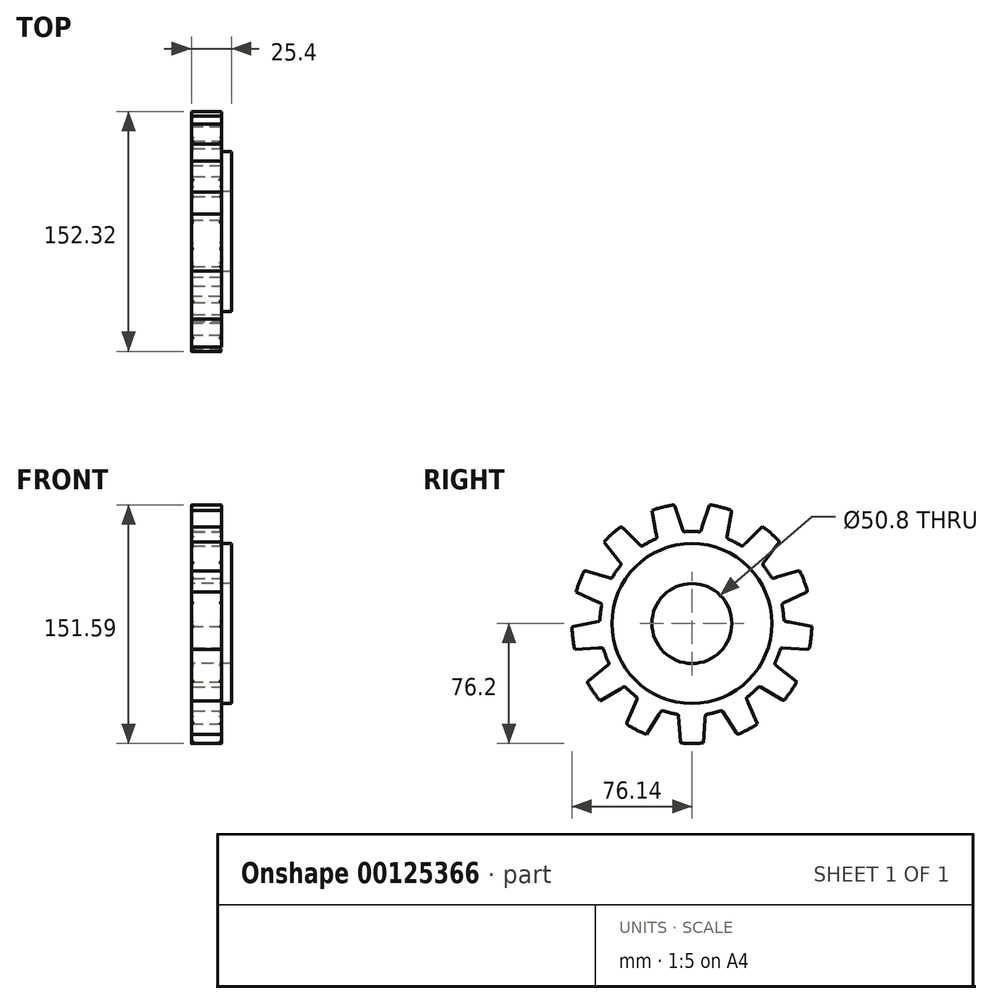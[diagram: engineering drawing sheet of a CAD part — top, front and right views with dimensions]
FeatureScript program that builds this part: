
annotation { "Feature Type Name" : "Feature", "Feature Type Description" : "" }
export const myFeature = defineFeature(function(context is Context, id is Id, definition is map)
    precondition{}
    {
        {
            var Q0;
            Q0=qCreatedBy(makeId("Front.planeOp"),FACE);
            var sketch = newSketch(context, id + "F0", { "sketchPlane" : qUnion([Q0])});
            skLineSegment(sketch, "E0.bottom", {"start": v(-41.26, 25.4) * mm, "end": v(-22.2, 25.4) * mm});
            skLineSegment(sketch, "E0.left", {"start": v(-41.26, 25.4) * mm, "end": v(-41.26, -25.4) * mm});
            skLineSegment(sketch, "E0.right", {"start": v(-22.2, 25.4) * mm, "end": v(-22.2, 0) * mm});
            skLineSegment(sketch, "E1.top", {"start": v(-22.2, 0) * mm, "end": v(-15.86, 0) * mm});
            skLineSegment(sketch, "E1.right", {"start": v(-15.86, -25.4) * mm, "end": v(-15.86, 0) * mm});
            skLineSegment(sketch, "E2", {"start": v(-57.48, -50.8) * mm, "end": v(16.42, -50.8) * mm});
            skLineSegment(sketch, "E3", {"start": v(-41.26, -25.4) * mm, "end": v(-15.86, -25.4) * mm});
            skSolve(sketch);
        }
        {
            var Q0;
            Q0=makeQuery(id+"F0.imprint","IMPRINT",FACE,{"disambiguationData":[TD([[makeQuery(id+"F0.imprint","IMPRINT",EDGE,{"derivedFrom":sQuery(id+"F0.wireOp",EDGE,"E0.bottom")}),-1.0]])]});
            var Q1;
            Q1=sQuery(id+"F0.wireOp",EDGE,"E2");
            revolve(context, id + "F1", {"entities" : qUnion([Q0]), "axis" : qUnion([Q1]), "revolveType" : RevolveType.FULL});
        }
        {
            var Q0;
            Q0=makeQuery(id+"F1.opRevolve","SWEPT_FACE",FACE,{"disambiguationData":[OSD([sQuery(id+"F0.wireOp",EDGE,"E0.right")])]});
            var sketch = newSketch(context, id + "F2", { "sketchPlane" : qUnion([Q0])});
            skLineSegment(sketch, "E4", {"start": v(-11.09, 24.59) * mm, "end": v(-5.53, 7.37) * mm});
            skLineSegment(sketch, "E5.MirrorCS", {"start": v(11.09, 24.59) * mm, "end": v(5.53, 7.37) * mm});
            skPoint(sketch, "E6.start.orphan", {"position": v(0, 25.4) * mm});
            skArc(sketch, "E7", {"start": v(5.53, 7.37) * mm, "mid": v(0, 7.63) * mm, "end": v(-5.53, 7.37) * mm});
            skSolve(sketch);
        }
        {
            var Q0;
            {var subQ0=sQuery(id+"F2.wireOp",EDGE,"E4");Q0=makeQuery(id+"F2.imprint","IMPRINT",FACE,{"disambiguationData":[TD([[makeQuery(id+"F2.imprint","IMPRINT",EDGE,{"derivedFrom":subQ0}),1.0]])]});}
            extrude(context, id + "F3", {"entities" : qUnion([Q0]), "operationType" : NewBodyOperationType.REMOVE, "oppositeDirection" : true, "depth" : 25.4 * mm});
        }
        {
            var Q0;
            Q0=makeQuery(id+"F3.boolean.opBoolean","COPY",FACE,{"derivedFrom":makeQuery(id+"F3.opExtrude","SWEPT_FACE",FACE,{"disambiguationData":[OSD([sQuery(id+"F2.wireOp",EDGE,"E4")])]})});
            var Q1;
            Q1=makeQuery(id+"F3.boolean.opBoolean","COPY",FACE,{"derivedFrom":makeQuery(id+"F3.opExtrude","SWEPT_FACE",FACE,{"disambiguationData":[OSD([sQuery(id+"F2.wireOp",EDGE,"E7")])]})});
            var Q2;
            Q2=makeQuery(id+"F3.boolean.opBoolean","INTERSECT",EDGE,{"derivedFrom":[makeQuery(id+"F1.opRevolve","SWEPT_FACE",FACE,{"disambiguationData":[OSD([sQuery(id+"F0.wireOp",EDGE,"E0.left")])]}),makeQuery(id+"F3.opExtrude","SWEPT_FACE",FACE,{"disambiguationData":[OSD([sQuery(id+"F2.wireOp",EDGE,"E7")])]})]});
            fillet(context, id + "F4", {"entities" : qUnion([Q0, Q1, Q2]), "radius" : 1.27 * mm, "tangentPropagation" : true, "allowEdgeOverflow" : false});
        }
        {
            var Q0;
            Q0=makeQuery(id+"F3.boolean.opBoolean","COPY",FACE,{"derivedFrom":makeQuery(id+"F3.opExtrude","SWEPT_FACE",FACE,{"disambiguationData":[OSD([sQuery(id+"F2.wireOp",EDGE,"E4")])]})});
            var Q1;
            Q1=makeQuery(id+"F4.opFillet","BLEND_FACE",FACE,{"disambiguationData":[OSD([sQuery(id+"F2.wireOp",EDGE,"E4")])]});
            var Q2;
            Q2=makeQuery(id+"F4.opFillet","BLEND_FACE",FACE,{"disambiguationData":[OSD([sQuery(id+"F0.wireOp",EDGE,"E0.bottom"),sQuery(id+"F0.wireOp",EDGE,"E0.right"),sQuery(id+"F2.wireOp",EDGE,"E4")])]});
            var Q3;
            {var subQ0=sQuery(id+"F2.wireOp",EDGE,"E7");var subQ1=sQuery(id+"F2.wireOp",EDGE,"E4");Q3=makeQuery(id+"F4.opFillet","BLEND_FACE",FACE,{"disambiguationData":[OSD([subQ1,subQ0]),TDD([makeQuery(id+"F3.boolean.opBoolean","COPY",EDGE,{"derivedFrom":makeQuery(id+"F3.opExtrude","SWEPT_EDGE",EDGE,{"disambiguationData":[OSD([subQ1,subQ0])]})})])]});}
            var Q4;
            {var subQ0=sQuery(id+"F2.wireOp",EDGE,"E7");var subQ1=sQuery(id+"F2.wireOp",EDGE,"E4");Q4=makeQuery(id+"F4.opFillet","BLEND_FACE",FACE,{"disambiguationData":[OSD([subQ1,subQ0]),TDD([makeQuery(id+"F3.boolean.opBoolean","COPY",VERTEX,{"derivedFrom":makeQuery(id+"F3.opExtrude","CAP_VERTEX",VERTEX,{"disambiguationData":[OSD([subQ1,subQ0])],"isStart":true})})])]});}
            var Q5;
            Q5=makeQuery(id+"F4.opFillet","BLEND_FACE",FACE,{"disambiguationData":[OSD([sQuery(id+"F2.wireOp",EDGE,"E7")])]});
            var Q6;
            Q6=makeQuery(id+"F3.boolean.opBoolean","COPY",FACE,{"derivedFrom":makeQuery(id+"F3.opExtrude","SWEPT_FACE",FACE,{"disambiguationData":[OSD([sQuery(id+"F2.wireOp",EDGE,"E7")])]})});
            var Q7;
            {var subQ0=sQuery(id+"F2.wireOp",EDGE,"E7");var subQ1=sQuery(id+"F2.wireOp",EDGE,"E5.MirrorCS");Q7=makeQuery(id+"F4.opFillet","BLEND_FACE",FACE,{"disambiguationData":[OSD([subQ1,subQ0]),TDD([makeQuery(id+"F3.boolean.opBoolean","COPY",EDGE,{"derivedFrom":makeQuery(id+"F3.opExtrude","SWEPT_EDGE",EDGE,{"disambiguationData":[OSD([subQ1,subQ0])]})})])]});}
            var Q8;
            Q8=makeQuery(id+"F4.opFillet","BLEND_FACE",FACE,{"disambiguationData":[OSD([sQuery(id+"F2.wireOp",EDGE,"E5.MirrorCS")])]});
            var Q9;
            {var subQ0=sQuery(id+"F2.wireOp",EDGE,"E7");var subQ1=sQuery(id+"F2.wireOp",EDGE,"E5.MirrorCS");Q9=makeQuery(id+"F4.opFillet","BLEND_FACE",FACE,{"disambiguationData":[OSD([subQ1,subQ0]),TDD([makeQuery(id+"F3.boolean.opBoolean","COPY",VERTEX,{"derivedFrom":makeQuery(id+"F3.opExtrude","CAP_VERTEX",VERTEX,{"disambiguationData":[OSD([subQ1,subQ0])],"isStart":true})})])]});}
            var Q10;
            Q10=makeQuery(id+"F3.boolean.opBoolean","COPY",FACE,{"derivedFrom":makeQuery(id+"F3.opExtrude","SWEPT_FACE",FACE,{"disambiguationData":[OSD([sQuery(id+"F2.wireOp",EDGE,"E5.MirrorCS")])]})});
            var Q11;
            Q11=makeQuery(id+"F4.opFillet","BLEND_FACE",FACE,{"disambiguationData":[OSD([sQuery(id+"F0.wireOp",EDGE,"E0.left"),sQuery(id+"F2.wireOp",EDGE,"E5.MirrorCS")])]});
            var Q12;
            Q12=makeQuery(id+"F4.opFillet","BLEND_FACE",FACE,{"disambiguationData":[OSD([sQuery(id+"F0.wireOp",EDGE,"E0.left"),sQuery(id+"F2.wireOp",EDGE,"E5.MirrorCS"),sQuery(id+"F2.wireOp",EDGE,"E7")])]});
            var Q13;
            Q13=makeQuery(id+"F4.opFillet","BLEND_FACE",FACE,{"disambiguationData":[OSD([sQuery(id+"F0.wireOp",EDGE,"E0.left"),sQuery(id+"F2.wireOp",EDGE,"E7")])]});
            var Q14;
            Q14=makeQuery(id+"F4.opFillet","BLEND_FACE",FACE,{"disambiguationData":[OSD([sQuery(id+"F0.wireOp",EDGE,"E0.left"),sQuery(id+"F2.wireOp",EDGE,"E4"),sQuery(id+"F2.wireOp",EDGE,"E7")])]});
            var Q15;
            Q15=makeQuery(id+"F4.opFillet","BLEND_FACE",FACE,{"disambiguationData":[OSD([sQuery(id+"F0.wireOp",EDGE,"E0.left"),sQuery(id+"F2.wireOp",EDGE,"E4")])]});
            var Q16;
            Q16=sQuery(id+"F0.wireOp",EDGE,"E2");
            circularPattern(context, id + "F5", {"patternType" : PatternType.FACE, "faces" : qUnion([Q0, Q1, Q2, Q3, Q4, Q5, Q6, Q7, Q8, Q9, Q10, Q11, Q12, Q13, Q14, Q15]), "axis" : qUnion([Q16]), "angle" : 360 * degree, "instanceCount" : 13, "equalSpace" : true});
        }
    });
